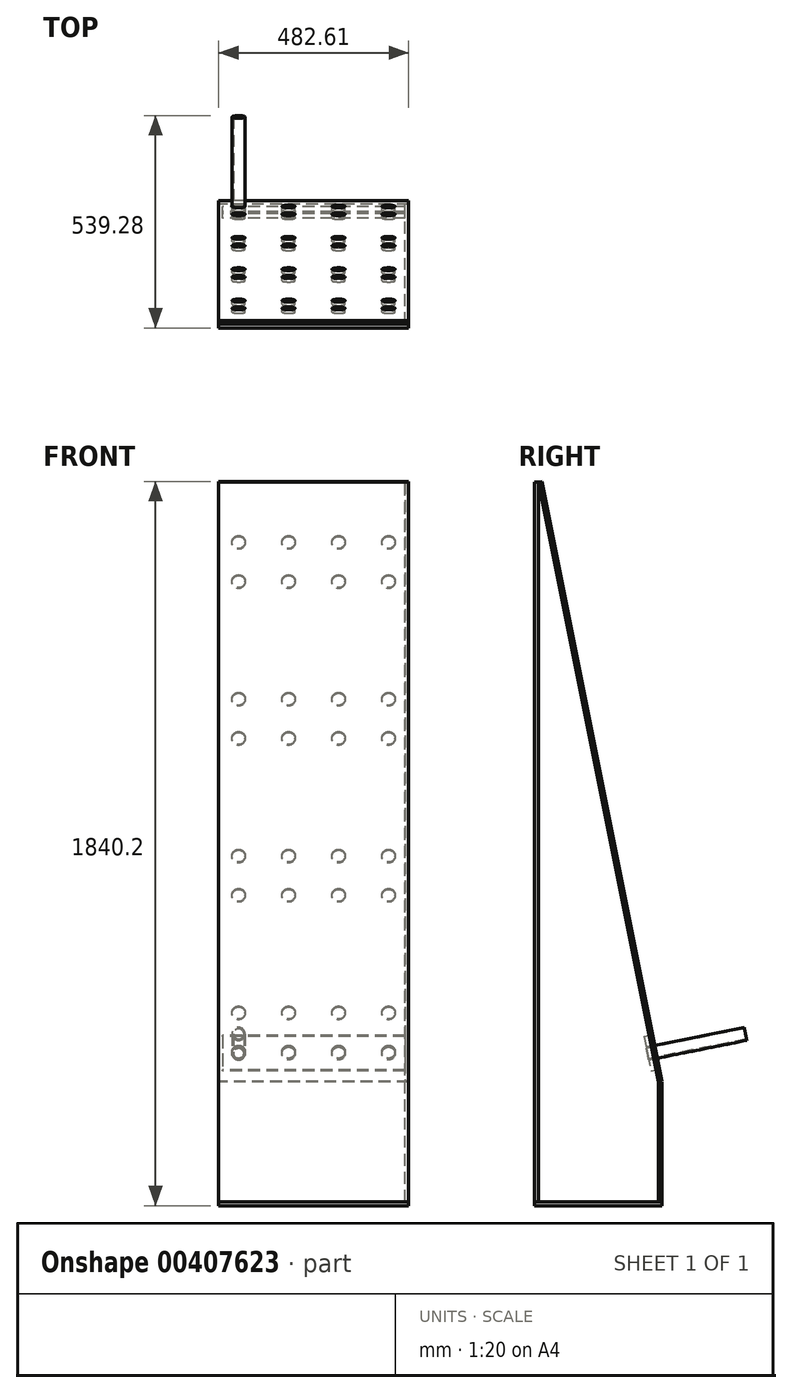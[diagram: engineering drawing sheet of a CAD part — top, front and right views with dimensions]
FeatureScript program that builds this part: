
annotation { "Feature Type Name" : "Feature", "Feature Type Description" : "" }
export const myFeature = defineFeature(function(context is Context, id is Id, definition is map)
    precondition{}
    {
        {
            var Q0;
            Q0=qCreatedBy(makeId("Right.planeOp"),FACE);
            var sketch = newSketch(context, id + "F0", { "sketchPlane" : qUnion([Q0])});
            skLineSegment(sketch, "E0.bottom", {"start": v(0, 0) * mm, "end": v(304.8, 0) * mm});
            skLineSegment(sketch, "E0.top", {"start": v(0, 1828.8) * mm, "end": v(0, 1828.8) * mm});
            skLineSegment(sketch, "E0.left", {"start": v(0, 0) * mm, "end": v(0, 1828.8) * mm});
            skLineSegment(sketch, "E0.right", {"start": v(304.8, 0) * mm, "end": v(304.8, 304.8) * mm});
            skLineSegment(sketch, "E1", {"start": v(0, 1828.8) * mm, "end": v(304.8, 304.8) * mm});
            skPoint(sketch, "E2.orphan", {"position": v(304.8, 1828.8) * mm});
            skSolve(sketch);
        }
        {
            var Q0;
            Q0 = qSketchRegion(id + "F0", true);
            extrude(context, id + "F1", {"entities" : qUnion([Q0]), "depth" : 9.52 * mm});
        }
        {
            var Q0;
            Q0=makeQuery(id+"F1.opExtrude","SWEPT_FACE",FACE,{"disambiguationData":[OSD([sQuery(id+"F0.wireOp",EDGE,"E0.right")])]});
            var sketch = newSketch(context, id + "F2", { "sketchPlane" : qUnion([Q0])});
            skLineSegment(sketch, "E3.bottom", {"start": v(-9.53, 304.8) * mm, "end": v(473.08, 304.8) * mm});
            skLineSegment(sketch, "E3.top", {"start": v(-9.53, 0) * mm, "end": v(473.08, 0) * mm});
            skLineSegment(sketch, "E3.left", {"start": v(-9.53, 304.8) * mm, "end": v(-9.52, 0) * mm});
            skLineSegment(sketch, "E3.right", {"start": v(473.08, 304.8) * mm, "end": v(473.08, 0) * mm});
            skSolve(sketch);
        }
        {
            var Q0;
            Q0 = qSketchRegion(id + "F2", true);
            extrude(context, id + "F3", {"entities" : qUnion([Q0]), "depth" : 9.52 * mm});
        }
        {
            var Q0;
            Q0=makeQuery(id+"F1.opExtrude","SWEPT_FACE",FACE,{"disambiguationData":[OSD([sQuery(id+"F0.wireOp",EDGE,"E1")])]});
            var sketch = newSketch(context, id + "F4", { "sketchPlane" : qUnion([Q0])});
            skLineSegment(sketch, "E4.bottom", {"start": v(-9.53, 1793.29) * mm, "end": v(473.08, 1793.29) * mm});
            skLineSegment(sketch, "E4.top", {"start": v(-9.53, 239.1) * mm, "end": v(473.08, 239.1) * mm});
            skLineSegment(sketch, "E4.left", {"start": v(-9.53, 1793.29) * mm, "end": v(-9.52, 239.1) * mm});
            skLineSegment(sketch, "E4.right", {"start": v(473.08, 1793.29) * mm, "end": v(473.08, 239.1) * mm});
            skSolve(sketch);
        }
        {
            var Q0;
            Q0 = qSketchRegion(id + "F4", true);
            extrude(context, id + "F5", {"entities" : qUnion([Q0]), "depth" : 9.52 * mm});
        }
        {
            var Q0;
            Q0=makeQuery(id+"F1.opExtrude","SWEPT_FACE",FACE,{"disambiguationData":[OSD([sQuery(id+"F0.wireOp",EDGE,"E0.left")])]});
            var sketch = newSketch(context, id + "F6", { "sketchPlane" : qUnion([Q0])});
            skLineSegment(sketch, "E5.bottom", {"start": v(9.53, 0) * mm, "end": v(-473.08, 0) * mm});
            skLineSegment(sketch, "E5.top", {"start": v(9.52, 1828.8) * mm, "end": v(-473.08, 1828.8) * mm});
            skLineSegment(sketch, "E5.left", {"start": v(9.53, 0) * mm, "end": v(9.53, 1828.8) * mm});
            skLineSegment(sketch, "E5.right", {"start": v(-473.08, 0) * mm, "end": v(-473.08, 1828.8) * mm});
            skSolve(sketch);
        }
        {
            var Q0;
            Q0 = qSketchRegion(id + "F6", true);
            extrude(context, id + "F7", {"entities" : qUnion([Q0]), "depth" : 9.52 * mm});
        }
        {
            var Q0;
            Q0=makeQuery(id+"F3.opExtrude","SWEPT_FACE",FACE,{"disambiguationData":[OSD([sQuery(id+"F2.wireOp",EDGE,"E3.top")])]});
            var sketch = newSketch(context, id + "F8", { "sketchPlane" : qUnion([Q0])});
            skLineSegment(sketch, "E6.bottom", {"start": v(-473.08, -314.33) * mm, "end": v(9.53, -314.33) * mm});
            skLineSegment(sketch, "E6.top", {"start": v(-473.08, 9.53) * mm, "end": v(9.52, 9.53) * mm});
            skLineSegment(sketch, "E6.left", {"start": v(-473.08, -314.33) * mm, "end": v(-473.08, 9.53) * mm});
            skLineSegment(sketch, "E6.right", {"start": v(9.53, -314.33) * mm, "end": v(9.52, 9.53) * mm});
            skSolve(sketch);
        }
        {
            var Q0;
            Q0 = qSketchRegion(id + "F8", true);
            extrude(context, id + "F9", {"entities" : qUnion([Q0]), "depth" : 9.52 * mm});
        }
        {
            var Q0;
            Q0=makeQuery(id+"F5.opExtrude","CAP_FACE",FACE,{"disambiguationData":[OSD([sQuery(id+"F4.wireOp",EDGE,"E4.bottom"),sQuery(id+"F4.wireOp",EDGE,"E4.top"),sQuery(id+"F4.wireOp",EDGE,"E4.left"),sQuery(id+"F4.wireOp",EDGE,"E4.right")])],"isStart":false});
            var sketch = newSketch(context, id + "F10", { "sketchPlane" : qUnion([Q0])});
            skCircle(sketch, "E7", {"center": v(41.28, 315.3) * mm, "radius": 16.76 * mm});
            skCircle(sketch, "E8.0.1.0", {"center": v(41.28, 416.9) * mm, "radius": 16.76 * mm});
            skCircle(sketch, "E8.1.0.0", {"center": v(168.28, 315.3) * mm, "radius": 16.76 * mm});
            skCircle(sketch, "E8.1.1.0", {"center": v(168.28, 416.9) * mm, "radius": 16.76 * mm});
            skCircle(sketch, "E8.2.0.0", {"center": v(295.28, 315.3) * mm, "radius": 16.76 * mm});
            skCircle(sketch, "E8.2.1.0", {"center": v(295.28, 416.9) * mm, "radius": 16.76 * mm});
            skCircle(sketch, "E8.3.0.0", {"center": v(422.28, 315.3) * mm, "radius": 16.76 * mm});
            skCircle(sketch, "E8.3.1.0", {"center": v(422.28, 416.9) * mm, "radius": 16.76 * mm});
            skLineSegment(sketch, "E8.direction1", {"start": v(41.28, 315.3) * mm, "end": v(168.28, 315.3) * mm, "construction": true});
            skLineSegment(sketch, "E8.direction2", {"start": v(41.28, 315.3) * mm, "end": v(41.28, 416.9) * mm, "construction": true});
            skCircle(sketch, "E9.0.1.0", {"center": v(422.28, 721.7) * mm, "radius": 16.76 * mm});
            skCircle(sketch, "E9.0.1.1", {"center": v(422.28, 823.3) * mm, "radius": 16.76 * mm});
            skLineSegment(sketch, "E9.0.1.2", {"start": v(41.28, 721.7) * mm, "end": v(41.28, 823.3) * mm, "construction": true});
            skCircle(sketch, "E9.0.1.3", {"center": v(168.28, 721.7) * mm, "radius": 16.76 * mm});
            skCircle(sketch, "E9.0.1.4", {"center": v(168.28, 823.3) * mm, "radius": 16.76 * mm});
            skCircle(sketch, "E9.0.1.5", {"center": v(295.28, 721.7) * mm, "radius": 16.76 * mm});
            skCircle(sketch, "E9.0.1.6", {"center": v(41.28, 823.3) * mm, "radius": 16.76 * mm});
            skCircle(sketch, "E9.0.1.7", {"center": v(41.28, 721.7) * mm, "radius": 16.76 * mm});
            skLineSegment(sketch, "E9.0.1.8", {"start": v(41.28, 721.7) * mm, "end": v(168.28, 721.7) * mm, "construction": true});
            skCircle(sketch, "E9.0.1.9", {"center": v(295.28, 823.3) * mm, "radius": 16.76 * mm});
            skCircle(sketch, "E9.0.2.0", {"center": v(422.28, 1128.1) * mm, "radius": 16.76 * mm});
            skCircle(sketch, "E9.0.2.1", {"center": v(422.28, 1229.7) * mm, "radius": 16.76 * mm});
            skLineSegment(sketch, "E9.0.2.2", {"start": v(41.28, 1128.1) * mm, "end": v(41.28, 1229.7) * mm, "construction": true});
            skCircle(sketch, "E9.0.2.3", {"center": v(168.28, 1128.1) * mm, "radius": 16.76 * mm});
            skCircle(sketch, "E9.0.2.4", {"center": v(168.28, 1229.7) * mm, "radius": 16.76 * mm});
            skCircle(sketch, "E9.0.2.5", {"center": v(295.28, 1128.1) * mm, "radius": 16.76 * mm});
            skCircle(sketch, "E9.0.2.6", {"center": v(41.28, 1229.7) * mm, "radius": 16.76 * mm});
            skCircle(sketch, "E9.0.2.7", {"center": v(41.28, 1128.1) * mm, "radius": 16.76 * mm});
            skLineSegment(sketch, "E9.0.2.8", {"start": v(41.28, 1128.1) * mm, "end": v(168.28, 1128.1) * mm, "construction": true});
            skCircle(sketch, "E9.0.2.9", {"center": v(295.28, 1229.7) * mm, "radius": 16.76 * mm});
            skCircle(sketch, "E9.0.3.0", {"center": v(422.28, 1534.5) * mm, "radius": 16.76 * mm});
            skCircle(sketch, "E9.0.3.1", {"center": v(422.28, 1636.1) * mm, "radius": 16.76 * mm});
            skLineSegment(sketch, "E9.0.3.2", {"start": v(41.28, 1534.5) * mm, "end": v(41.28, 1636.1) * mm, "construction": true});
            skCircle(sketch, "E9.0.3.3", {"center": v(168.28, 1534.5) * mm, "radius": 16.76 * mm});
            skCircle(sketch, "E9.0.3.4", {"center": v(168.28, 1636.1) * mm, "radius": 16.76 * mm});
            skCircle(sketch, "E9.0.3.5", {"center": v(295.28, 1534.5) * mm, "radius": 16.76 * mm});
            skCircle(sketch, "E9.0.3.6", {"center": v(41.28, 1636.1) * mm, "radius": 16.76 * mm});
            skCircle(sketch, "E9.0.3.7", {"center": v(41.28, 1534.5) * mm, "radius": 16.76 * mm});
            skLineSegment(sketch, "E9.0.3.8", {"start": v(41.28, 1534.5) * mm, "end": v(168.28, 1534.5) * mm, "construction": true});
            skCircle(sketch, "E9.0.3.9", {"center": v(295.28, 1636.1) * mm, "radius": 16.76 * mm});
            skLineSegment(sketch, "E9.direction1", {"start": v(41.28, 315.3) * mm, "end": v(620.4, 315.3) * mm, "construction": true});
            skLineSegment(sketch, "E9.direction2", {"start": v(41.28, 315.3) * mm, "end": v(41.28, 721.7) * mm, "construction": true});
            skSolve(sketch);
        }
        {
            var Q0;
            Q0 = qSketchRegion(id + "F10", true);
            extrude(context, id + "F11", {"entities" : qUnion([Q0]), "operationType" : NewBodyOperationType.REMOVE, "oppositeDirection" : true, "depth" : 12.7 * mm});
        }
        {
            var Q0;
            Q0=makeQuery(id+"F5.opExtrude","CAP_FACE",FACE,{"disambiguationData":[OSD([sQuery(id+"F4.wireOp",EDGE,"E4.bottom"),sQuery(id+"F4.wireOp",EDGE,"E4.top"),sQuery(id+"F4.wireOp",EDGE,"E4.left"),sQuery(id+"F4.wireOp",EDGE,"E4.right")])],"isStart":true});
            var sketch = newSketch(context, id + "F12", { "sketchPlane" : qUnion([Q0])});
            skLineSegment(sketch, "E10.bottom", {"start": v(0, 359.75) * mm, "end": v(-463.55, 359.75) * mm});
            skLineSegment(sketch, "E10.top", {"start": v(0, 270.85) * mm, "end": v(-463.55, 270.85) * mm});
            skLineSegment(sketch, "E10.left", {"start": v(0, 359.75) * mm, "end": v(0, 270.85) * mm});
            skLineSegment(sketch, "E10.right", {"start": v(-463.55, 359.75) * mm, "end": v(-463.55, 270.85) * mm});
            skCircle(sketch, "E11", {"center": v(-41.28, 315.3) * mm, "radius": 16.76 * mm});
            skCircle(sketch, "E12", {"center": v(-168.28, 315.3) * mm, "radius": 16.76 * mm});
            skCircle(sketch, "E13", {"center": v(-295.28, 315.3) * mm, "radius": 16.76 * mm});
            skCircle(sketch, "E14", {"center": v(-422.28, 315.3) * mm, "radius": 16.76 * mm});
            skSolve(sketch);
        }
        {
            var Q0;
            Q0 = qSketchRegion(id + "F12", true);
            extrude(context, id + "F13", {"entities" : qUnion([Q0]), "depth" : 12.7 * mm});
        }
        {
            var Q0;
            Q0=makeQuery(id+"F13.opExtrude","CAP_FACE",FACE,{"disambiguationData":[OSD([sQuery(id+"F12.wireOp",EDGE,"E10.bottom"),sQuery(id+"F12.wireOp",EDGE,"E10.top"),sQuery(id+"F12.wireOp",EDGE,"E10.left"),sQuery(id+"F12.wireOp",EDGE,"E10.right"),sQuery(id+"F12.wireOp",EDGE,"E11"),sQuery(id+"F12.wireOp",EDGE,"E12"),sQuery(id+"F12.wireOp",EDGE,"E13"),sQuery(id+"F12.wireOp",EDGE,"E14")])],"isStart":false});
            var sketch = newSketch(context, id + "F14", { "sketchPlane" : qUnion([Q0])});
            skCircle(sketch, "E15", {"center": v(-422.28, 315.3) * mm, "radius": 16.7 * mm});
            skCircle(sketch, "E16", {"center": v(-422.28, 315.3) * mm, "radius": 13.34 * mm});
            skSolve(sketch);
        }
        {
            var Q0;
            Q0 = qSketchRegion(id + "F14", true);
            extrude(context, id + "F15", {"entities" : qUnion([Q0]), "oppositeDirection" : true, "depth" : 254 * mm});
        }
    });
